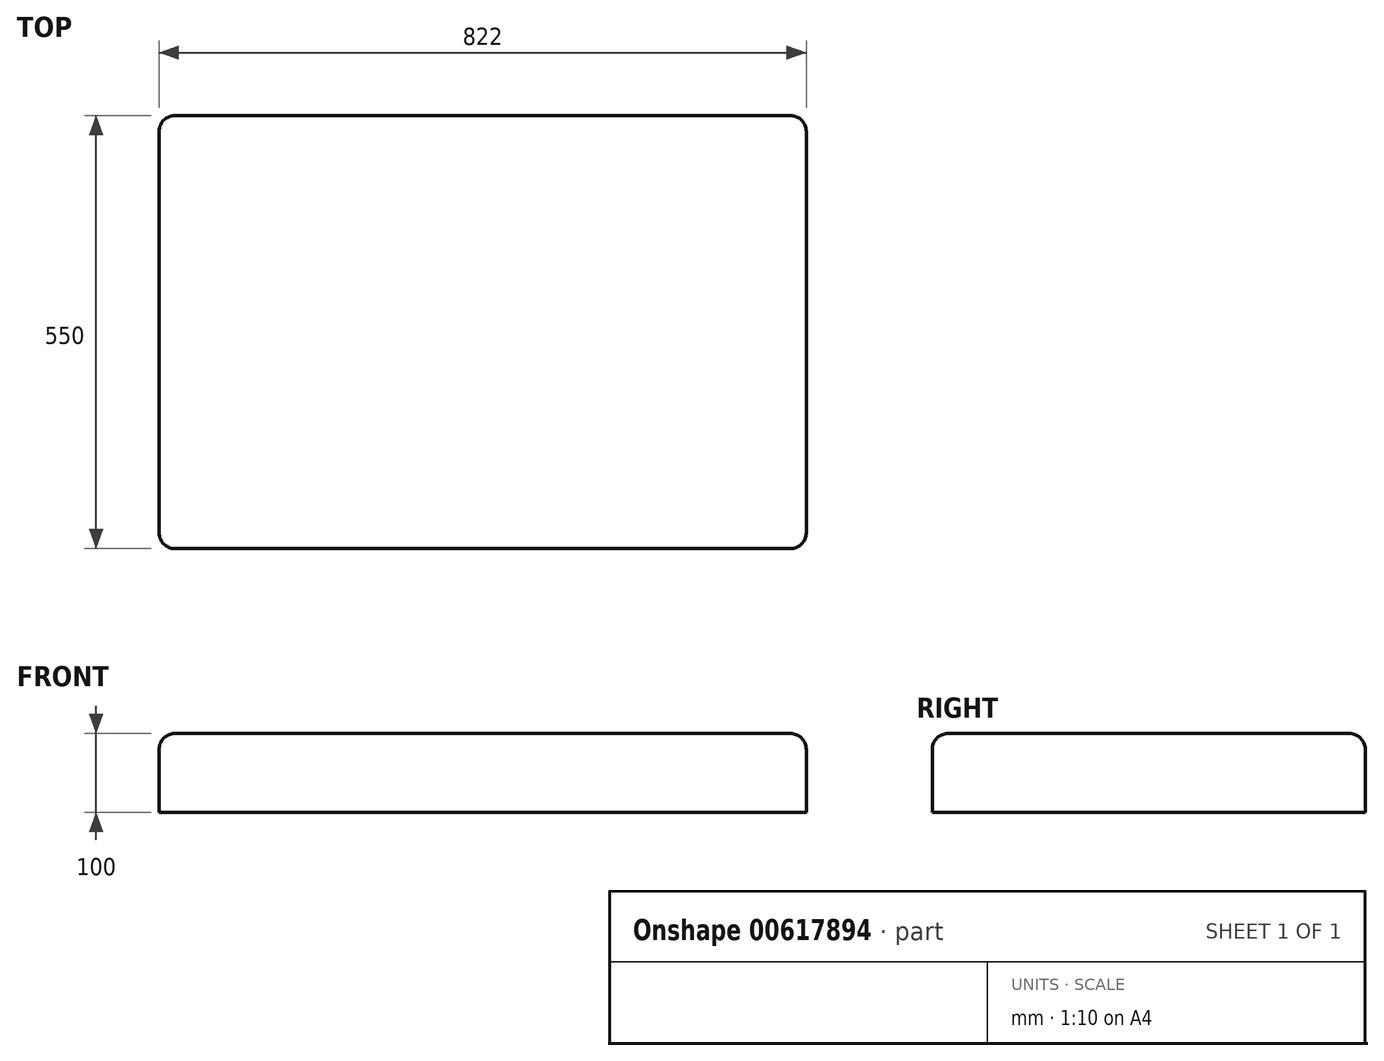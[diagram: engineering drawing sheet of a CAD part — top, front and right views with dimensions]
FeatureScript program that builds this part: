
annotation { "Feature Type Name" : "Feature", "Feature Type Description" : "" }
export const myFeature = defineFeature(function(context is Context, id is Id, definition is map)
    precondition{}
    {
        {
            var Q0;
            Q0=qCreatedBy(makeId("Top.planeOp"),FACE);
            var sketch = newSketch(context, id + "F0", { "sketchPlane" : qUnion([Q0])});
            skLineSegment(sketch, "E0.bottom", {"start": v(411, -273.64) * mm, "end": v(-411, -273.64) * mm});
            skLineSegment(sketch, "E0.top", {"start": v(411, 276.36) * mm, "end": v(-411, 276.36) * mm});
            skLineSegment(sketch, "E0.left", {"start": v(411, -273.64) * mm, "end": v(411, 276.36) * mm});
            skLineSegment(sketch, "E0.right", {"start": v(-411, -273.64) * mm, "end": v(-411, 276.36) * mm});
            skPoint(sketch, "E0.middle", {"position": v(0, 1.36) * mm});
            skSolve(sketch);
        }
        {
            var Q0;
            Q0 = qSketchRegion(id + "F0", true);
            extrude(context, id + "F1", {"entities" : qUnion([Q0]), "depth" : 100 * mm, "offsetDistance" : 25 * mm});
        }
        {
            var Q0;
            Q0=makeQuery(id+"F1.opExtrude","CAP_EDGE",EDGE,{"disambiguationData":[OSD([sQuery(id+"F0.wireOp",EDGE,"E0.bottom")])],"isStart":false});
            var Q1;
            Q1=makeQuery(id+"F1.opExtrude","CAP_EDGE",EDGE,{"disambiguationData":[OSD([sQuery(id+"F0.wireOp",EDGE,"E0.right")])],"isStart":false});
            var Q2;
            Q2=makeQuery(id+"F1.opExtrude","CAP_EDGE",EDGE,{"disambiguationData":[OSD([sQuery(id+"F0.wireOp",EDGE,"E0.top")])],"isStart":false});
            var Q3;
            Q3=makeQuery(id+"F1.opExtrude","CAP_EDGE",EDGE,{"disambiguationData":[OSD([sQuery(id+"F0.wireOp",EDGE,"E0.left")])],"isStart":false});
            var Q4;
            Q4=makeQuery(id+"F1.opExtrude","SWEPT_EDGE",EDGE,{"disambiguationData":[OSD([sQuery(id+"F0.wireOp",EDGE,"E0.bottom"),sQuery(id+"F0.wireOp",EDGE,"E0.left")])]});
            var Q5;
            Q5=makeQuery(id+"F1.opExtrude","SWEPT_EDGE",EDGE,{"disambiguationData":[OSD([sQuery(id+"F0.wireOp",EDGE,"E0.top"),sQuery(id+"F0.wireOp",EDGE,"E0.left")])]});
            var Q6;
            Q6=makeQuery(id+"F1.opExtrude","SWEPT_EDGE",EDGE,{"disambiguationData":[OSD([sQuery(id+"F0.wireOp",EDGE,"E0.bottom"),sQuery(id+"F0.wireOp",EDGE,"E0.right")])]});
            var Q7;
            Q7=makeQuery(id+"F1.opExtrude","SWEPT_EDGE",EDGE,{"disambiguationData":[OSD([sQuery(id+"F0.wireOp",EDGE,"E0.top"),sQuery(id+"F0.wireOp",EDGE,"E0.right")])]});
            fillet(context, id + "F2", {"entities" : qUnion([Q0, Q1, Q2, Q3, Q4, Q5, Q6, Q7]), "radius" : 20 * mm, "tangentPropagation" : true, "allowEdgeOverflow" : false});
        }
    });
